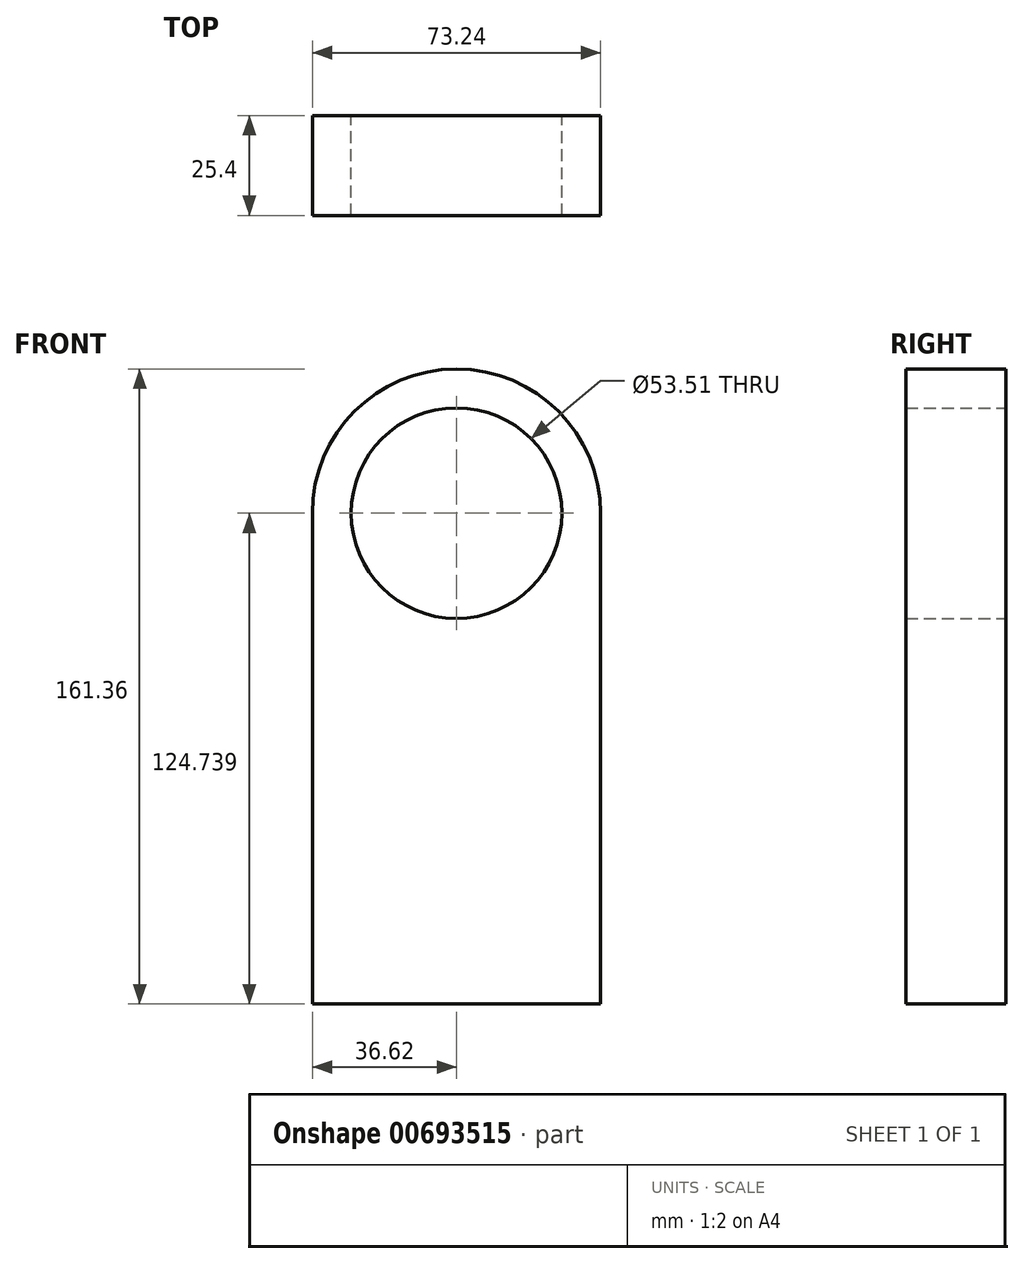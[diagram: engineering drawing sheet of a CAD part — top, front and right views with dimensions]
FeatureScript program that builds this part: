
annotation { "Feature Type Name" : "Feature", "Feature Type Description" : "" }
export const myFeature = defineFeature(function(context is Context, id is Id, definition is map)
    precondition{}
    {
        {
            var Q0;
            Q0=qCreatedBy(makeId("Front.planeOp"),FACE);
            var sketch = newSketch(context, id + "F0", { "sketchPlane" : qUnion([Q0])});
            skLineSegment(sketch, "E0.top", {"start": v(-36.62, -62.37) * mm, "end": v(36.62, -62.37) * mm});
            skLineSegment(sketch, "E0.left", {"start": v(-36.62, 62.37) * mm, "end": v(-36.62, -62.37) * mm});
            skLineSegment(sketch, "E0.right", {"start": v(36.62, 62.37) * mm, "end": v(36.62, -62.37) * mm});
            skPoint(sketch, "E0.middle", {"position": v(0, 0) * mm});
            skArc(sketch, "E1", {"start": v(36.62, 62.37) * mm, "mid": v(0, 99) * mm, "end": v(-36.62, 62.37) * mm});
            skCircle(sketch, "E2", {"center": v(0, 62.37) * mm, "radius": 26.75 * mm});
            skSolve(sketch);
        }
        {
            var Q0;
            Q0=makeQuery(id+"F0.imprint","IMPRINT",FACE,{"disambiguationData":[TD([[makeQuery(id+"F0.imprint","IMPRINT",EDGE,{"derivedFrom":sQuery(id+"F0.wireOp",EDGE,"E0.top")}),1.0]])]});
            extrude(context, id + "F1", {"entities" : qUnion([Q0]), "depth" : 25.4 * mm, "offsetDistance" : 25.4 * mm});
        }
    });
